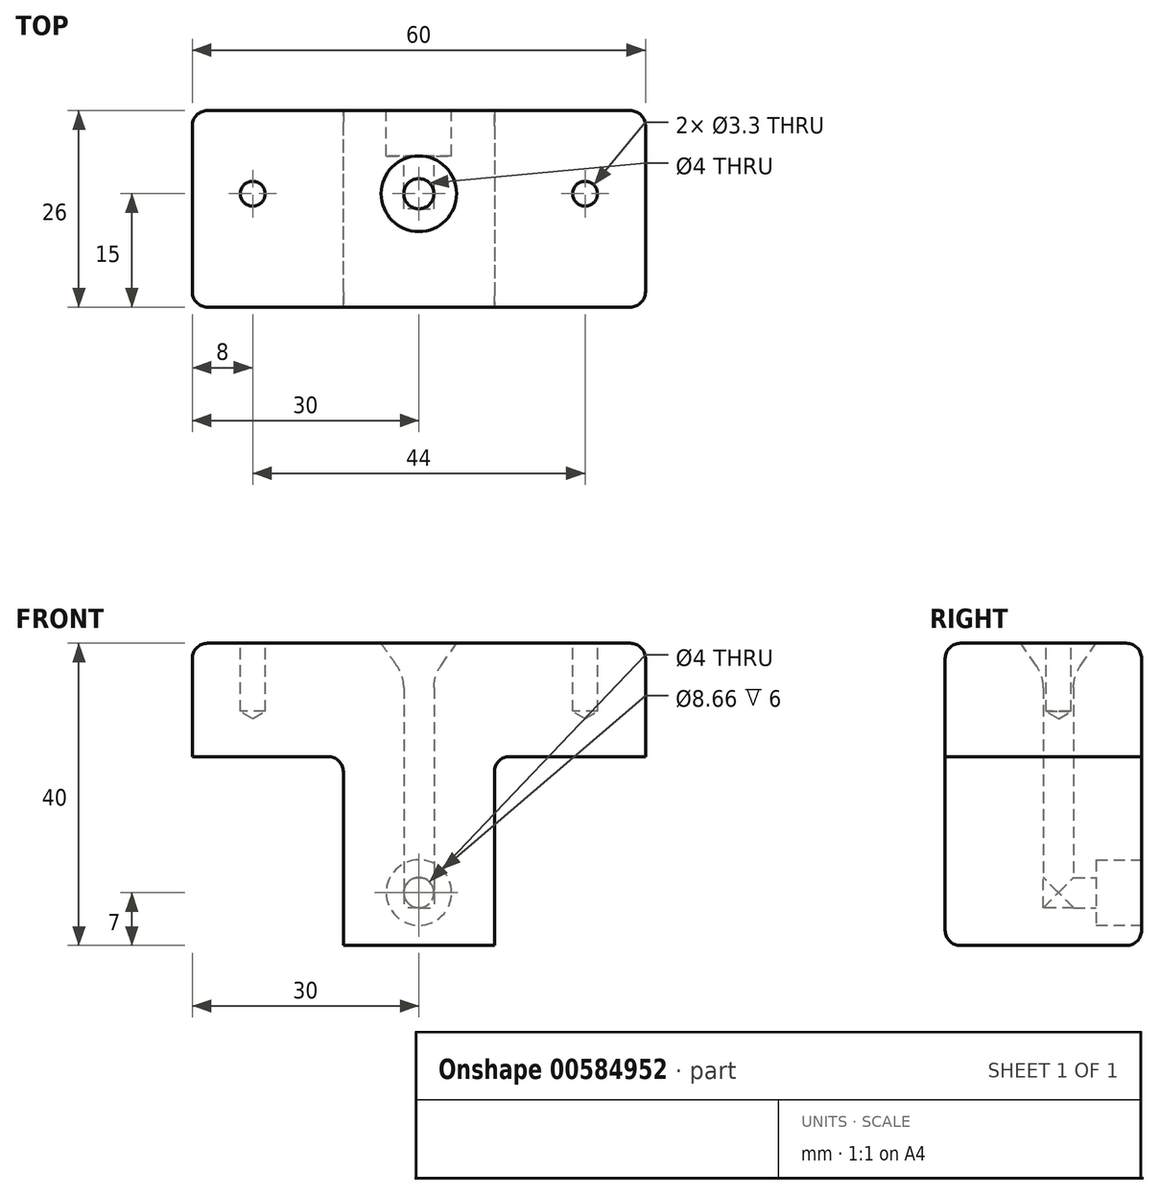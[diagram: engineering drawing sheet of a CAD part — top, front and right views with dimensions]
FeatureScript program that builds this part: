
annotation { "Feature Type Name" : "Feature", "Feature Type Description" : "" }
export const myFeature = defineFeature(function(context is Context, id is Id, definition is map)
    precondition{}
    {
        {
            var Q0;
            Q0=qCreatedBy(makeId("Top.planeOp"),FACE);
            var sketch = newSketch(context, id + "F0", { "sketchPlane" : qUnion([Q0])});
            skLineSegment(sketch, "E0.bottom", {"start": v(0, 0) * mm, "end": v(60, 0) * mm});
            skLineSegment(sketch, "E0.top", {"start": v(0, 26) * mm, "end": v(60, 26) * mm});
            skLineSegment(sketch, "E0.left", {"start": v(0, 0) * mm, "end": v(0, 26) * mm});
            skLineSegment(sketch, "E0.right", {"start": v(60, 0) * mm, "end": v(60, 26) * mm});
            skSolve(sketch);
        }
        {
            var Q0;
            Q0=makeQuery(id+"F0.imprint","IMPRINT",FACE,{"disambiguationData":[TD([[makeQuery(id+"F0.imprint","IMPRINT",EDGE,{"derivedFrom":sQuery(id+"F0.wireOp",EDGE,"E0.bottom")}),1.0]])]});
            extrude(context, id + "F1", {"entities" : qUnion([Q0]), "depth" : 40 * mm, "offsetDistance" : 25 * mm});
        }
        {
            var Q0;
            Q0=qCreatedBy(makeId("Front.planeOp"),FACE);
            cPlane(context, id + "F2", {"entities" : qUnion([Q0]), "cplaneType" : CPlaneType.OFFSET, "offset" : 15 * mm, "oppositeDirection" : true, "width" : 150 * mm, "height" : 150 * mm});
        }
        {
            var Q0;
            Q0=qCreatedBy(id+"F2.planeOp",FACE);
            var sketch = newSketch(context, id + "F3", { "sketchPlane" : qUnion([Q0])});
            skLineSegment(sketch, "E1", {"start": v(30, 40) * mm, "end": v(30, 5) * mm});
            skLineSegment(sketch, "E2", {"start": v(30, 40) * mm, "end": v(35, 40) * mm});
            skLineSegment(sketch, "E3", {"start": v(35, 40) * mm, "end": v(32.9, 37) * mm});
            skLineSegment(sketch, "E4", {"start": v(32, 34.13) * mm, "end": v(32, 5) * mm});
            skPoint(sketch, "E5.visualSharp", {"position": v(32, 35.7) * mm});
            skArc(sketch, "E5.filletArc", {"start": v(32.9, 37) * mm, "mid": v(32.23, 35.64) * mm, "end": v(32, 34.13) * mm});
            skLineSegment(sketch, "E6", {"start": v(32, 5) * mm, "end": v(30, 5) * mm});
            skSolve(sketch);
        }
        {
            var Q0;
            Q0 = qSketchRegion(id + "F3", true);
            var Q1;
            Q1=sQuery(id+"F3.wireOp",EDGE,"E1");
            revolve(context, id + "F4", {"operationType" : NewBodyOperationType.REMOVE, "entities" : qUnion([Q0]), "axis" : qUnion([Q1]), "revolveType" : RevolveType.FULL, "oppositeDirection" : true});
        }
        {
            var Q0;
            Q0=makeQuery(id+"F1.opExtrude","SWEPT_FACE",FACE,{"disambiguationData":[OSD([sQuery(id+"F0.wireOp",EDGE,"E0.top")])]});
            var sketch = newSketch(context, id + "F5", { "sketchPlane" : qUnion([Q0])});
            skCircle(sketch, "E7", {"center": v(-30, 7) * mm, "radius": 2 * mm});
            skSolve(sketch);
        }
        {
            var Q0;
            Q0 = qSketchRegion(id + "F5", true);
            extrude(context, id + "F6", {"entities" : qUnion([Q0]), "operationType" : NewBodyOperationType.REMOVE, "oppositeDirection" : true, "depth" : 13 * mm, "offsetDistance" : 25 * mm});
        }
        {
            var Q0;
            Q0=makeQuery(id+"F1.opExtrude","CAP_FACE",FACE,{"disambiguationData":[OSD([sQuery(id+"F0.wireOp",EDGE,"E0.bottom"),sQuery(id+"F0.wireOp",EDGE,"E0.top"),sQuery(id+"F0.wireOp",EDGE,"E0.left"),sQuery(id+"F0.wireOp",EDGE,"E0.right")])],"isStart":false});
            var sketch = newSketch(context, id + "F7", { "sketchPlane" : qUnion([Q0])});
            skLineSegment(sketch, "E8", {"start": v(8, 15) * mm, "end": v(52, 15) * mm, "construction": true});
            skPoint(sketch, "E9", {"position": v(8, 15) * mm});
            skPoint(sketch, "E10", {"position": v(52, 15) * mm});
            skSolve(sketch);
        }
        {
            var Q0;
            Q0=sQuery(id+"F7.wireOp",VERTEX,"E9");
            var Q1;
            Q1=sQuery(id+"F7.wireOp",VERTEX,"E10");
            var Q2;
            Q2=makeQuery(id+"F1.opExtrude","SWEPT_BODY",BODY,{"disambiguationData":[OSD([sQuery(id+"F0.wireOp",EDGE,"E0.bottom"),sQuery(id+"F0.wireOp",EDGE,"E0.top"),sQuery(id+"F0.wireOp",EDGE,"E0.left"),sQuery(id+"F0.wireOp",EDGE,"E0.right")])]});
            hole(context, id + "F8", {"style" : HoleStyle.SIMPLE, "endStyle" : HoleEndStyle.BLIND, "standardTappedOrClearance" : lookupTablePath({ "standard" : "ISO", "fit" : "Normal", "size" : "M3", "type" : "Clearance" }), "standardBlindInLast" : lookupTablePath({ "fit" : "Standard", "standard" : "ISO", "size" : "M3", "type" : "Clearance" }), "holeDiameter" : 3.3 * mm, "majorDiameter" : 5 * mm, "holeDepth" : 9 * mm, "isTappedThrough" : true, "tappedDepth" : 7 * mm, "tapClearance" : 2, "startFromSketch" : true, "locations" : qUnion([Q0, Q1]), "scope" : qUnion([Q2])});
        }
        {
            var Q0;
            Q0=makeQuery(id+"F1.opExtrude","SWEPT_FACE",FACE,{"disambiguationData":[OSD([sQuery(id+"F0.wireOp",EDGE,"E0.top")])]});
            var sketch = newSketch(context, id + "F9", { "sketchPlane" : qUnion([Q0])});
            skCircle(sketch, "E11", {"center": v(-30, 7) * mm, "radius": 4.33 * mm});
            skSolve(sketch);
        }
        {
            var Q0;
            Q0 = qSketchRegion(id + "F9", true);
            extrude(context, id + "F10", {"entities" : qUnion([Q0]), "operationType" : NewBodyOperationType.REMOVE, "oppositeDirection" : true, "depth" : 6 * mm, "offsetDistance" : 25 * mm});
        }
        {
            var Q0;
            Q0=makeQuery(id+"F1.opExtrude","CAP_FACE",FACE,{"disambiguationData":[OSD([sQuery(id+"F0.wireOp",EDGE,"E0.bottom"),sQuery(id+"F0.wireOp",EDGE,"E0.top"),sQuery(id+"F0.wireOp",EDGE,"E0.left"),sQuery(id+"F0.wireOp",EDGE,"E0.right")])],"isStart":true});
            var sketch = newSketch(context, id + "F11", { "sketchPlane" : qUnion([Q0])});
            skLineSegment(sketch, "E12.bottom", {"start": v(0, 0) * mm, "end": v(20, 0) * mm});
            skLineSegment(sketch, "E12.top", {"start": v(0, -26) * mm, "end": v(20, -26) * mm});
            skLineSegment(sketch, "E12.left", {"start": v(0, 0) * mm, "end": v(0, -26) * mm});
            skLineSegment(sketch, "E12.right", {"start": v(20, 0) * mm, "end": v(20, -26) * mm});
            skLineSegment(sketch, "E13.bottom", {"start": v(60, -26) * mm, "end": v(40, -26) * mm});
            skLineSegment(sketch, "E13.top", {"start": v(60, 0) * mm, "end": v(40, 0) * mm});
            skLineSegment(sketch, "E13.left", {"start": v(60, -26) * mm, "end": v(60, 0) * mm});
            skLineSegment(sketch, "E13.right", {"start": v(40, -26) * mm, "end": v(40, 0) * mm});
            skSolve(sketch);
        }
        {
            var Q0;
            Q0 = qSketchRegion(id + "F11", true);
            extrude(context, id + "F12", {"entities" : qUnion([Q0]), "operationType" : NewBodyOperationType.REMOVE, "oppositeDirection" : true, "depth" : 25 * mm, "offsetDistance" : 25 * mm});
        }
        {
            var Q0;
            Q0=makeQuery(id+"F1.opExtrude","CAP_EDGE",EDGE,{"disambiguationData":[OSD([sQuery(id+"F0.wireOp",EDGE,"E0.top")])],"isStart":false});
            var Q1;
            Q1=makeQuery(id+"F1.opExtrude","CAP_EDGE",EDGE,{"disambiguationData":[OSD([sQuery(id+"F0.wireOp",EDGE,"E0.bottom")])],"isStart":false});
            var Q2;
            Q2=makeQuery(id+"F1.opExtrude","CAP_EDGE",EDGE,{"disambiguationData":[OSD([sQuery(id+"F0.wireOp",EDGE,"E0.right")])],"isStart":false});
            var Q3;
            Q3=makeQuery(id+"F1.opExtrude","CAP_EDGE",EDGE,{"disambiguationData":[OSD([sQuery(id+"F0.wireOp",EDGE,"E0.left")])],"isStart":false});
            var Q4;
            Q4=makeQuery(id+"F1.opExtrude","SWEPT_EDGE",EDGE,{"disambiguationData":[OSD([sQuery(id+"F0.wireOp",EDGE,"E0.bottom"),sQuery(id+"F0.wireOp",EDGE,"E0.left")])]});
            var Q5;
            Q5=makeQuery(id+"F12.boolean.opBoolean","COPY",EDGE,{"derivedFrom":makeQuery(id+"F12.opExtrude","CAP_EDGE",EDGE,{"disambiguationData":[OSD([sQuery(id+"F11.wireOp",EDGE,"E12.bottom")])],"isStart":false})});
            var Q6;
            Q6=makeQuery(id+"F12.boolean.opBoolean","COPY",EDGE,{"derivedFrom":makeQuery(id+"F12.opExtrude","CAP_EDGE",EDGE,{"disambiguationData":[OSD([sQuery(id+"F11.wireOp",EDGE,"E12.left")])],"isStart":false})});
            var Q7;
            Q7=makeQuery(id+"F12.boolean.opBoolean","COPY",EDGE,{"derivedFrom":makeQuery(id+"F12.opExtrude","SWEPT_EDGE",EDGE,{"disambiguationData":[OSD([sQuery(id+"F0.wireOp",EDGE,"E0.bottom"),sQuery(id+"F11.wireOp",EDGE,"E12.bottom"),sQuery(id+"F11.wireOp",EDGE,"E12.right")])]})});
            var Q8;
            Q8=makeQuery(id+"F12.boolean.opBoolean","COPY",EDGE,{"derivedFrom":makeQuery(id+"F12.opExtrude","CAP_EDGE",EDGE,{"disambiguationData":[OSD([sQuery(id+"F11.wireOp",EDGE,"E12.right")])],"isStart":false})});
            var Q9;
            Q9=makeQuery(id+"F12.boolean.opBoolean","COPY",EDGE,{"derivedFrom":makeQuery(id+"F12.opExtrude","SWEPT_EDGE",EDGE,{"disambiguationData":[OSD([sQuery(id+"F0.wireOp",EDGE,"E0.top"),sQuery(id+"F11.wireOp",EDGE,"E12.top"),sQuery(id+"F11.wireOp",EDGE,"E12.right")])]})});
            var Q10;
            Q10=makeQuery(id+"F12.boolean.opBoolean","COPY",EDGE,{"derivedFrom":makeQuery(id+"F12.opExtrude","CAP_EDGE",EDGE,{"disambiguationData":[OSD([sQuery(id+"F11.wireOp",EDGE,"E12.right")])],"isStart":true})});
            var Q11;
            Q11=makeQuery(id+"F1.opExtrude","CAP_EDGE",EDGE,{"disambiguationData":[OSD([sQuery(id+"F0.wireOp",EDGE,"E0.top")])],"isStart":true});
            var Q12;
            Q12=makeQuery(id+"F1.opExtrude","CAP_EDGE",EDGE,{"disambiguationData":[OSD([sQuery(id+"F0.wireOp",EDGE,"E0.bottom")])],"isStart":true});
            var Q13;
            Q13=makeQuery(id+"F12.boolean.opBoolean","COPY",EDGE,{"derivedFrom":makeQuery(id+"F12.opExtrude","CAP_EDGE",EDGE,{"disambiguationData":[OSD([sQuery(id+"F11.wireOp",EDGE,"E13.right")])],"isStart":true})});
            var Q14;
            Q14=makeQuery(id+"F12.boolean.opBoolean","COPY",EDGE,{"derivedFrom":makeQuery(id+"F12.opExtrude","SWEPT_EDGE",EDGE,{"disambiguationData":[OSD([sQuery(id+"F0.wireOp",EDGE,"E0.top"),sQuery(id+"F11.wireOp",EDGE,"E13.bottom"),sQuery(id+"F11.wireOp",EDGE,"E13.right")])]})});
            var Q15;
            Q15=makeQuery(id+"F12.boolean.opBoolean","COPY",EDGE,{"derivedFrom":makeQuery(id+"F12.opExtrude","CAP_EDGE",EDGE,{"disambiguationData":[OSD([sQuery(id+"F11.wireOp",EDGE,"E13.right")])],"isStart":false})});
            var Q16;
            Q16=makeQuery(id+"F12.boolean.opBoolean","COPY",EDGE,{"derivedFrom":makeQuery(id+"F12.opExtrude","CAP_EDGE",EDGE,{"disambiguationData":[OSD([sQuery(id+"F11.wireOp",EDGE,"E13.bottom")])],"isStart":false})});
            var Q17;
            Q17=makeQuery(id+"F12.boolean.opBoolean","COPY",EDGE,{"derivedFrom":makeQuery(id+"F12.opExtrude","CAP_EDGE",EDGE,{"disambiguationData":[OSD([sQuery(id+"F11.wireOp",EDGE,"E13.left")])],"isStart":false})});
            var Q18;
            Q18=makeQuery(id+"F12.boolean.opBoolean","COPY",EDGE,{"derivedFrom":makeQuery(id+"F12.opExtrude","CAP_EDGE",EDGE,{"disambiguationData":[OSD([sQuery(id+"F11.wireOp",EDGE,"E13.top")])],"isStart":false})});
            var Q19;
            Q19=makeQuery(id+"F12.boolean.opBoolean","COPY",EDGE,{"derivedFrom":makeQuery(id+"F12.opExtrude","SWEPT_EDGE",EDGE,{"disambiguationData":[OSD([sQuery(id+"F0.wireOp",EDGE,"E0.bottom"),sQuery(id+"F11.wireOp",EDGE,"E13.top"),sQuery(id+"F11.wireOp",EDGE,"E13.right")])]})});
            var Q20;
            Q20=makeQuery(id+"F1.opExtrude","SWEPT_EDGE",EDGE,{"disambiguationData":[OSD([sQuery(id+"F0.wireOp",EDGE,"E0.top"),sQuery(id+"F0.wireOp",EDGE,"E0.right")])]});
            var Q21;
            Q21=makeQuery(id+"F1.opExtrude","SWEPT_EDGE",EDGE,{"disambiguationData":[OSD([sQuery(id+"F0.wireOp",EDGE,"E0.bottom"),sQuery(id+"F0.wireOp",EDGE,"E0.right")])]});
            var Q22;
            Q22=makeQuery(id+"F1.opExtrude","SWEPT_EDGE",EDGE,{"disambiguationData":[OSD([sQuery(id+"F0.wireOp",EDGE,"E0.top"),sQuery(id+"F0.wireOp",EDGE,"E0.left")])]});
            fillet(context, id + "F13", {"entities" : qUnion([Q0, Q1, Q2, Q3, Q4, Q5, Q6, Q7, Q8, Q9, Q10, Q11, Q12, Q13, Q14, Q15, Q16, Q17, Q18, Q19, Q20, Q21, Q22]), "radius" : 2 * mm, "tangentPropagation" : true, "allowEdgeOverflow" : false});
        }
    });
